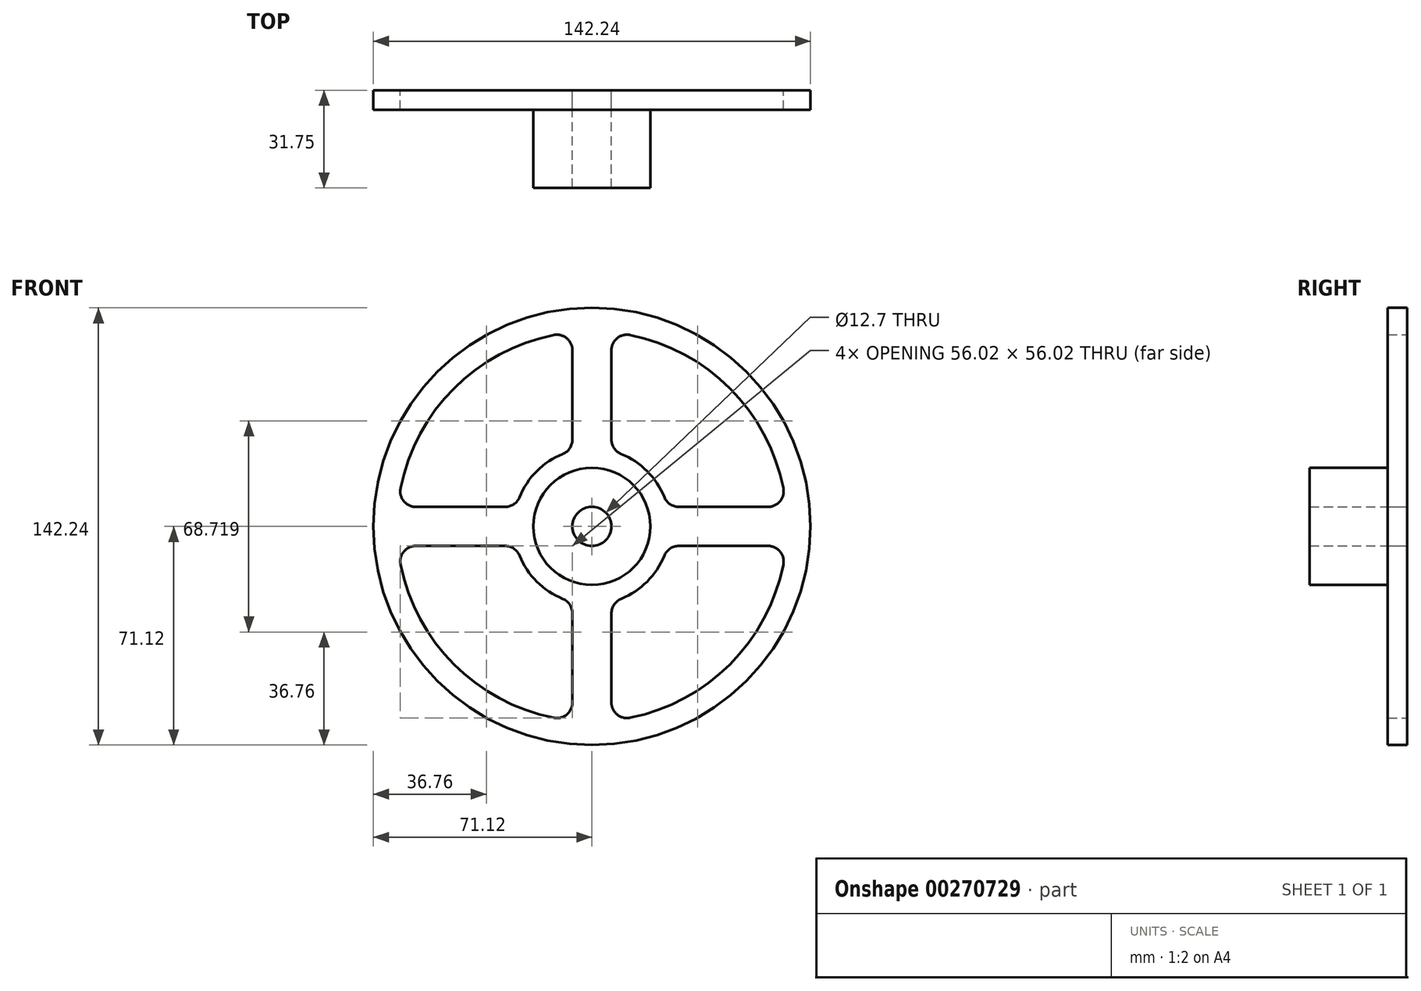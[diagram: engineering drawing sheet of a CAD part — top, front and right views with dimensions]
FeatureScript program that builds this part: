
annotation { "Feature Type Name" : "Feature", "Feature Type Description" : "" }
export const myFeature = defineFeature(function(context is Context, id is Id, definition is map)
    precondition{}
    {
        {
            var Q0;
            Q0=qCreatedBy(makeId("Front.planeOp"),FACE);
            var sketch = newSketch(context, id + "F0", { "sketchPlane" : qUnion([Q0])});
            skCircle(sketch, "E0", {"center": v(0, 0) * mm, "radius": 71.12 * mm});
            skArc(sketch, "E1", {"start": v(62.27, 12.42) * mm, "mid": v(44.9, 44.9) * mm, "end": v(12.42, 62.27) * mm});
            skCircle(sketch, "E2", {"center": v(0, 0) * mm, "radius": 6.35 * mm});
            skArc(sketch, "E3", {"start": v(-23.55, -9.52) * mm, "mid": v(-17.96, -17.96) * mm, "end": v(-9.53, -23.55) * mm});
            skPoint(sketch, "E4.middle", {"position": v(-63.5, 0) * mm});
            skLineSegment(sketch, "E5.bottom", {"start": v(28.26, 6.35) * mm, "end": v(57.3, 6.35) * mm});
            skLineSegment(sketch, "E5.top", {"start": v(28.26, -6.35) * mm, "end": v(57.3, -6.35) * mm});
            skPoint(sketch, "E5.middle", {"position": v(63.5, 0) * mm});
            skArc(sketch, "E6.trimOffspring", {"start": v(-62.27, -12.42) * mm, "mid": v(-44.9, -44.9) * mm, "end": v(-12.42, -62.27) * mm});
            skLineSegment(sketch, "E7.trimOffspring", {"start": v(-28.26, -6.35) * mm, "end": v(-57.3, -6.35) * mm});
            skLineSegment(sketch, "E8.trimOffspring", {"start": v(-28.26, 6.35) * mm, "end": v(-57.3, 6.35) * mm});
            skPoint(sketch, "E9.orphan", {"position": v(0, 6.35) * mm});
            skArc(sketch, "E10.trimOffspring", {"start": v(23.55, 9.53) * mm, "mid": v(17.96, 17.96) * mm, "end": v(9.52, 23.55) * mm});
            skPoint(sketch, "E11.middle", {"position": v(0, 63.5) * mm});
            skPoint(sketch, "E12.middle", {"position": v(0, -63.5) * mm});
            skLineSegment(sketch, "E13.trimOffspring", {"start": v(-6.35, -28.26) * mm, "end": v(-6.35, -57.3) * mm});
            skLineSegment(sketch, "E14.trimOffspring", {"start": v(6.35, -28.26) * mm, "end": v(6.35, -57.3) * mm});
            skLineSegment(sketch, "E15.trimOffspring", {"start": v(-6.35, 28.26) * mm, "end": v(-6.35, 57.3) * mm});
            skLineSegment(sketch, "E16.trimOffspring", {"start": v(6.35, 28.26) * mm, "end": v(6.35, 57.3) * mm});
            skArc(sketch, "E17.trimOffspring", {"start": v(-9.53, 23.55) * mm, "mid": v(-17.96, 17.96) * mm, "end": v(-23.55, 9.52) * mm});
            skArc(sketch, "E18.trimOffspring", {"start": v(-12.42, 62.27) * mm, "mid": v(-44.9, 44.9) * mm, "end": v(-62.27, 12.42) * mm});
            skArc(sketch, "E19.trimOffspring", {"start": v(9.52, -23.55) * mm, "mid": v(17.96, -17.96) * mm, "end": v(23.55, -9.52) * mm});
            skArc(sketch, "E20.trimOffspring", {"start": v(12.42, -62.27) * mm, "mid": v(44.9, -44.9) * mm, "end": v(62.27, -12.42) * mm});
            skPoint(sketch, "E21.visualSharp", {"position": v(-6.35, -24.6) * mm});
            skArc(sketch, "E21.filletArc", {"start": v(-6.35, -28.26) * mm, "mid": v(-7.22, -25.42) * mm, "end": v(-9.53, -23.55) * mm});
            skPoint(sketch, "E22.visualSharp", {"position": v(-24.6, -6.35) * mm});
            skArc(sketch, "E22.filletArc", {"start": v(-23.55, -9.52) * mm, "mid": v(-25.42, -7.22) * mm, "end": v(-28.26, -6.35) * mm});
            skPoint(sketch, "E23.visualSharp", {"position": v(-63.18, -6.35) * mm});
            skArc(sketch, "E23.filletArc", {"start": v(-57.3, -6.35) * mm, "mid": v(-61.22, -8.2) * mm, "end": v(-62.27, -12.42) * mm});
            skPoint(sketch, "E24.visualSharp", {"position": v(-6.35, -63.18) * mm});
            skArc(sketch, "E24.filletArc", {"start": v(-12.42, -62.27) * mm, "mid": v(-8.2, -61.22) * mm, "end": v(-6.35, -57.3) * mm});
            skPoint(sketch, "E25.visualSharp", {"position": v(6.35, -63.18) * mm});
            skArc(sketch, "E25.filletArc", {"start": v(6.35, -57.3) * mm, "mid": v(8.2, -61.22) * mm, "end": v(12.42, -62.27) * mm});
            skPoint(sketch, "E26.visualSharp", {"position": v(6.35, -24.6) * mm});
            skArc(sketch, "E26.filletArc", {"start": v(9.52, -23.55) * mm, "mid": v(7.22, -25.42) * mm, "end": v(6.35, -28.26) * mm});
            skPoint(sketch, "E27.visualSharp", {"position": v(24.6, -6.35) * mm});
            skArc(sketch, "E27.filletArc", {"start": v(28.26, -6.35) * mm, "mid": v(25.42, -7.22) * mm, "end": v(23.55, -9.52) * mm});
            skPoint(sketch, "E28.visualSharp", {"position": v(63.18, -6.35) * mm});
            skArc(sketch, "E28.filletArc", {"start": v(62.27, -12.42) * mm, "mid": v(61.22, -8.2) * mm, "end": v(57.3, -6.35) * mm});
            skPoint(sketch, "E29.visualSharp", {"position": v(24.6, 6.35) * mm});
            skArc(sketch, "E29.filletArc", {"start": v(23.55, 9.52) * mm, "mid": v(25.42, 7.22) * mm, "end": v(28.26, 6.35) * mm});
            skPoint(sketch, "E30.visualSharp", {"position": v(63.18, 6.35) * mm});
            skArc(sketch, "E30.filletArc", {"start": v(57.3, 6.35) * mm, "mid": v(61.22, 8.2) * mm, "end": v(62.27, 12.42) * mm});
            skPoint(sketch, "E31.visualSharp", {"position": v(6.35, 24.6) * mm});
            skArc(sketch, "E31.filletArc", {"start": v(6.35, 28.26) * mm, "mid": v(7.22, 25.42) * mm, "end": v(9.52, 23.55) * mm});
            skPoint(sketch, "E32.visualSharp", {"position": v(-6.35, 24.6) * mm});
            skArc(sketch, "E32.filletArc", {"start": v(-9.53, 23.55) * mm, "mid": v(-7.22, 25.42) * mm, "end": v(-6.35, 28.26) * mm});
            skPoint(sketch, "E33.visualSharp", {"position": v(-24.6, 6.35) * mm});
            skArc(sketch, "E33.filletArc", {"start": v(-28.26, 6.35) * mm, "mid": v(-25.42, 7.22) * mm, "end": v(-23.55, 9.52) * mm});
            skPoint(sketch, "E34.visualSharp", {"position": v(-63.18, 6.35) * mm});
            skArc(sketch, "E34.filletArc", {"start": v(-62.27, 12.42) * mm, "mid": v(-61.22, 8.2) * mm, "end": v(-57.3, 6.35) * mm});
            skPoint(sketch, "E35.visualSharp", {"position": v(-6.35, 63.18) * mm});
            skArc(sketch, "E35.filletArc", {"start": v(-6.35, 57.3) * mm, "mid": v(-8.2, 61.22) * mm, "end": v(-12.42, 62.27) * mm});
            skPoint(sketch, "E36.visualSharp", {"position": v(6.35, 63.18) * mm});
            skArc(sketch, "E36.filletArc", {"start": v(12.42, 62.27) * mm, "mid": v(8.2, 61.22) * mm, "end": v(6.35, 57.3) * mm});
            skSolve(sketch);
        }
        {
            var Q0;
            Q0 = qSketchRegion(id + "F0", true);
            extrude(context, id + "F1", {"entities" : qUnion([Q0]), "depth" : 6.35 * mm});
        }
        {
            var Q0;
            Q0=makeQuery(id+"F1.opExtrude","CAP_FACE",FACE,{"disambiguationData":[OSD([sQuery(id+"F0.wireOp",EDGE,"E0"),sQuery(id+"F0.wireOp",EDGE,"E1"),sQuery(id+"F0.wireOp",EDGE,"E2"),sQuery(id+"F0.wireOp",EDGE,"E3"),sQuery(id+"F0.wireOp",EDGE,"E5.bottom"),sQuery(id+"F0.wireOp",EDGE,"E5.top"),sQuery(id+"F0.wireOp",EDGE,"E6.trimOffspring"),sQuery(id+"F0.wireOp",EDGE,"E7.trimOffspring"),sQuery(id+"F0.wireOp",EDGE,"E8.trimOffspring"),sQuery(id+"F0.wireOp",EDGE,"E10.trimOffspring"),sQuery(id+"F0.wireOp",EDGE,"E13.trimOffspring"),sQuery(id+"F0.wireOp",EDGE,"E14.trimOffspring"),sQuery(id+"F0.wireOp",EDGE,"E15.trimOffspring"),sQuery(id+"F0.wireOp",EDGE,"E16.trimOffspring"),sQuery(id+"F0.wireOp",EDGE,"E17.trimOffspring"),sQuery(id+"F0.wireOp",EDGE,"E18.trimOffspring"),sQuery(id+"F0.wireOp",EDGE,"E19.trimOffspring"),sQuery(id+"F0.wireOp",EDGE,"E20.trimOffspring"),sQuery(id+"F0.wireOp",EDGE,"E21.filletArc"),sQuery(id+"F0.wireOp",EDGE,"E22.filletArc"),sQuery(id+"F0.wireOp",EDGE,"E23.filletArc"),sQuery(id+"F0.wireOp",EDGE,"E24.filletArc"),sQuery(id+"F0.wireOp",EDGE,"E25.filletArc"),sQuery(id+"F0.wireOp",EDGE,"E26.filletArc"),sQuery(id+"F0.wireOp",EDGE,"E27.filletArc"),sQuery(id+"F0.wireOp",EDGE,"E28.filletArc"),sQuery(id+"F0.wireOp",EDGE,"E29.filletArc"),sQuery(id+"F0.wireOp",EDGE,"E30.filletArc"),sQuery(id+"F0.wireOp",EDGE,"E31.filletArc"),sQuery(id+"F0.wireOp",EDGE,"E32.filletArc"),sQuery(id+"F0.wireOp",EDGE,"E33.filletArc"),sQuery(id+"F0.wireOp",EDGE,"E34.filletArc"),sQuery(id+"F0.wireOp",EDGE,"E35.filletArc"),sQuery(id+"F0.wireOp",EDGE,"E36.filletArc")])],"isStart":false});
            var sketch = newSketch(context, id + "F2", { "sketchPlane" : qUnion([Q0])});
            skCircle(sketch, "E37", {"center": v(0, 0) * mm, "radius": 6.35 * mm});
            skCircle(sketch, "E38", {"center": v(0, 0) * mm, "radius": 19.05 * mm});
            skSolve(sketch);
        }
        {
            var Q0;
            Q0 = qSketchRegion(id + "F2", true);
            extrude(context, id + "F3", {"entities" : qUnion([Q0]), "operationType" : NewBodyOperationType.ADD, "depth" : 25.4 * mm});
        }
    });
